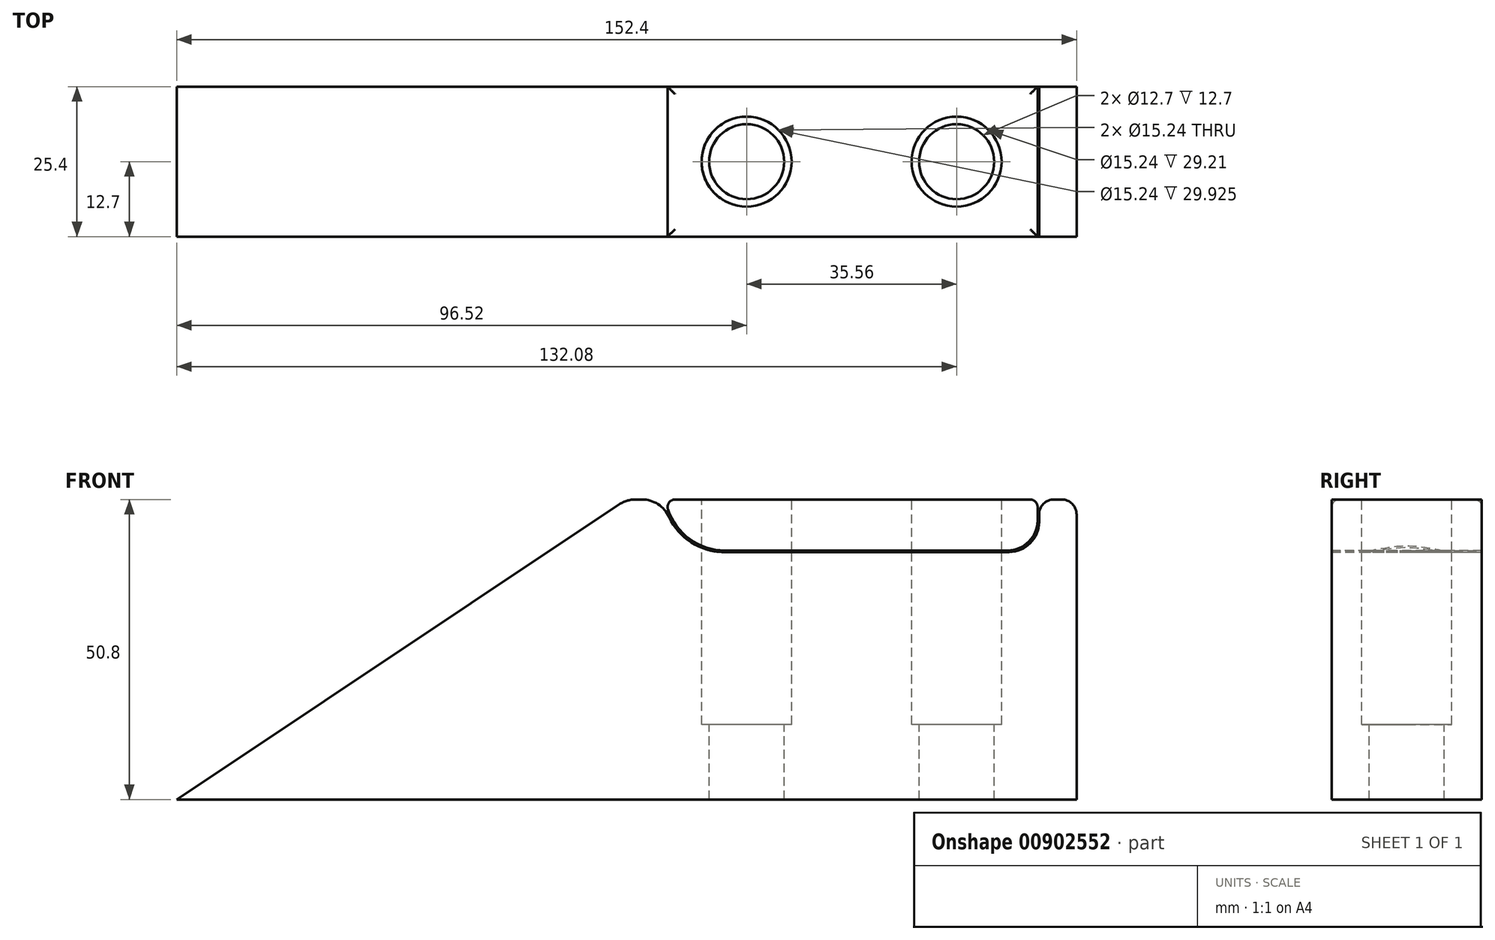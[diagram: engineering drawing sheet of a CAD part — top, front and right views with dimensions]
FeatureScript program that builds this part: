
annotation { "Feature Type Name" : "Feature", "Feature Type Description" : "" }
export const myFeature = defineFeature(function(context is Context, id is Id, definition is map)
    precondition{}
    {
        {
            var Q0;
            Q0=qCreatedBy(makeId("Front.planeOp"),FACE);
            var sketch = newSketch(context, id + "F0", { "sketchPlane" : qUnion([Q0])});
            skLineSegment(sketch, "E0.bottom", {"start": v(-76.2, -25.4) * mm, "end": v(76.2, -25.4) * mm});
            skLineSegment(sketch, "E0.right", {"start": v(76.2, -25.4) * mm, "end": v(76.2, 25.4) * mm});
            skPoint(sketch, "E0.middle", {"position": v(0, 0) * mm});
            skLineSegment(sketch, "E1", {"start": v(-76.2, -25.4) * mm, "end": v(0, 25.4) * mm});
            skLineSegment(sketch, "E2", {"start": v(6.35, 25.4) * mm, "end": v(6.35, 16.5) * mm});
            skLineSegment(sketch, "E3", {"start": v(6.35, 16.5) * mm, "end": v(69.85, 16.51) * mm});
            skLineSegment(sketch, "E4", {"start": v(69.85, 16.51) * mm, "end": v(69.85, 25.4) * mm});
            skLineSegment(sketch, "E5", {"start": v(0, 25.4) * mm, "end": v(6.35, 25.4) * mm});
            skLineSegment(sketch, "E6", {"start": v(69.85, 25.4) * mm, "end": v(76.2, 25.4) * mm});
            skLineSegment(sketch, "E7", {"start": v(6.6, 25.4) * mm, "end": v(6.6, 16.76) * mm});
            skLineSegment(sketch, "E8", {"start": v(6.6, 16.76) * mm, "end": v(69.6, 16.76) * mm});
            skLineSegment(sketch, "E9", {"start": v(69.6, 16.76) * mm, "end": v(69.6, 25.4) * mm});
            skLineSegment(sketch, "E10", {"start": v(6.6, 25.4) * mm, "end": v(69.6, 25.4) * mm});
            skSolve(sketch);
        }
        {
            var Q0;
            Q0=qSketchRegion(id+"F0",true);
            var Q1;
            Q1=makeQuery(id+"F0.imprint","IMPRINT",FACE,{"disambiguationData":[TD([[makeQuery(id+"F0.imprint","IMPRINT",EDGE,{"derivedFrom":sQuery(id+"F0.wireOp",EDGE,"E0.bottom")}),1.0]])]});
            extrude(context, id + "F1", {"entities" : qUnion([Q0, Q1]), "endBound" : BoundingType.SYMMETRIC, "depth" : 25.4 * mm, "offsetDistance" : 25.4 * mm});
        }
        {
            var Q0;
            Q0=makeQuery(id+"F1.opExtrude","SWEPT_FACE",FACE,{"disambiguationData":[OSD([sQuery(id+"F0.wireOp",EDGE,"E10")])]});
            var sketch = newSketch(context, id + "F2", { "sketchPlane" : qUnion([Q0])});
            skCircle(sketch, "E11", {"center": v(20.32, 0) * mm, "radius": 7.62 * mm});
            skCircle(sketch, "E12", {"center": v(55.88, 0) * mm, "radius": 7.62 * mm});
            skSolve(sketch);
        }
        {
            var Q0;
            Q0=makeQuery(id+"F2.imprint","IMPRINT",FACE,{"disambiguationData":[TD([[makeQuery(id+"F2.imprint","IMPRINT",EDGE,{"derivedFrom":sQuery(id+"F2.wireOp",EDGE,"E11")}),1.0]])]});
            var Q1;
            Q1=makeQuery(id+"F2.imprint","IMPRINT",FACE,{"disambiguationData":[TD([[makeQuery(id+"F2.imprint","IMPRINT",EDGE,{"derivedFrom":sQuery(id+"F2.wireOp",EDGE,"E12")}),1.0]])]});
            extrude(context, id + "F3", {"entities" : qUnion([Q0, Q1]), "operationType" : NewBodyOperationType.REMOVE, "oppositeDirection" : true, "depth" : 38.1 * mm, "offsetDistance" : 25.4 * mm});
        }
        {
            var Q0;
            Q0=makeQuery(id+"F1.opExtrude","SWEPT_FACE",FACE,{"disambiguationData":[OSD([sQuery(id+"F0.wireOp",EDGE,"E3")])]});
            var sketch = newSketch(context, id + "F4", { "sketchPlane" : qUnion([Q0])});
            skCircle(sketch, "E13", {"center": v(20.32, 0) * mm, "radius": 6.35 * mm});
            skCircle(sketch, "E14", {"center": v(55.88, 0) * mm, "radius": 6.35 * mm});
            skSolve(sketch);
        }
        {
            var Q0;
            Q0=makeQuery(id+"F4.imprint","IMPRINT",FACE,{"disambiguationData":[TD([[makeQuery(id+"F4.imprint","IMPRINT",EDGE,{"derivedFrom":sQuery(id+"F4.wireOp",EDGE,"E13")}),1.0]])]});
            var Q1;
            Q1=makeQuery(id+"F4.imprint","IMPRINT",FACE,{"disambiguationData":[TD([[makeQuery(id+"F4.imprint","IMPRINT",EDGE,{"derivedFrom":sQuery(id+"F4.wireOp",EDGE,"E14")}),1.0]])]});
            extrude(context, id + "F5", {"entities" : qUnion([Q0, Q1]), "operationType" : NewBodyOperationType.REMOVE, "oppositeDirection" : true, "depth" : 50.8 * mm, "offsetDistance" : 25.4 * mm});
        }
        {
            var Q0;
            Q0=makeQuery(id+"F1.opExtrude","SWEPT_EDGE",EDGE,{"disambiguationData":[OSD([sQuery(id+"F0.wireOp",EDGE,"E7"),sQuery(id+"F0.wireOp",EDGE,"E8")])]});
            fillet(context, id + "F6", {"entities" : qUnion([Q0]), "radius" : 10.16 * mm, "tangentPropagation" : true, "allowEdgeOverflow" : false});
        }
        {
            var Q0;
            Q0=makeQuery(id+"F1.opExtrude","SWEPT_EDGE",EDGE,{"disambiguationData":[OSD([sQuery(id+"F0.wireOp",EDGE,"E2"),sQuery(id+"F0.wireOp",EDGE,"E3")])]});
            fillet(context, id + "F7", {"entities" : qUnion([Q0]), "radius" : 10.16 * mm, "tangentPropagation" : true, "allowEdgeOverflow" : false});
        }
        {
            var Q0;
            Q0=makeQuery(id+"F7.opFillet","BLEND_EDGE",EDGE,{"blendedFrom":[makeQuery(id+"F1.opExtrude","SWEPT_EDGE",EDGE,{"disambiguationData":[OSD([sQuery(id+"F0.wireOp",EDGE,"E2"),sQuery(id+"F0.wireOp",EDGE,"E3")])]}),makeQuery(id+"F1.opExtrude","SWEPT_FACE",FACE,{"disambiguationData":[OSD([sQuery(id+"F0.wireOp",EDGE,"E5")])]})],"blendedInto":[makeQuery(id+"F1.opExtrude","SWEPT_FACE",FACE,{"disambiguationData":[OSD([sQuery(id+"F0.wireOp",EDGE,"E5")])]})]});
            var Q1;
            Q1=makeQuery(id+"F1.opExtrude","SWEPT_EDGE",EDGE,{"disambiguationData":[OSD([sQuery(id+"F0.wireOp",EDGE,"E1"),sQuery(id+"F0.wireOp",EDGE,"E5")])]});
            fillet(context, id + "F8", {"entities" : qUnion([Q0, Q1]), "radius" : 5.08 * mm, "tangentPropagation" : true, "allowEdgeOverflow" : false});
        }
        {
            var Q0;
            Q0=makeQuery(id+"F1.opExtrude","SWEPT_EDGE",EDGE,{"disambiguationData":[OSD([sQuery(id+"F0.wireOp",EDGE,"E0.right"),sQuery(id+"F0.wireOp",EDGE,"E6")])]});
            var Q1;
            Q1=makeQuery(id+"F1.opExtrude","SWEPT_EDGE",EDGE,{"disambiguationData":[OSD([sQuery(id+"F0.wireOp",EDGE,"E4"),sQuery(id+"F0.wireOp",EDGE,"E6")])]});
            fillet(context, id + "F9", {"entities" : qUnion([Q0, Q1]), "radius" : 2.54 * mm, "tangentPropagation" : true, "allowEdgeOverflow" : false});
        }
        {
            var Q0;
            Q0=makeQuery(id+"F1.opExtrude","SWEPT_EDGE",EDGE,{"disambiguationData":[OSD([sQuery(id+"F0.wireOp",EDGE,"E8"),sQuery(id+"F0.wireOp",EDGE,"E9")])]});
            fillet(context, id + "F10", {"entities" : qUnion([Q0]), "radius" : 5.08 * mm, "tangentPropagation" : true, "allowEdgeOverflow" : false});
        }
        {
            var Q0;
            Q0=makeQuery(id+"F1.opExtrude","SWEPT_EDGE",EDGE,{"disambiguationData":[OSD([sQuery(id+"F0.wireOp",EDGE,"E3"),sQuery(id+"F0.wireOp",EDGE,"E4")])]});
            fillet(context, id + "F11", {"entities" : qUnion([Q0]), "radius" : 5.08 * mm, "tangentPropagation" : true, "allowEdgeOverflow" : false});
        }
        {
            var Q0;
            Q0=makeQuery(id+"F1.opExtrude","CAP_EDGE",EDGE,{"disambiguationData":[OSD([sQuery(id+"F0.wireOp",EDGE,"E10")])],"isStart":true});
            var Q1;
            Q1=makeQuery(id+"F1.opExtrude","CAP_EDGE",EDGE,{"disambiguationData":[OSD([sQuery(id+"F0.wireOp",EDGE,"E10")])],"isStart":false});
            var Q2;
            Q2=makeQuery(id+"F1.opExtrude","SWEPT_EDGE",EDGE,{"disambiguationData":[OSD([sQuery(id+"F0.wireOp",EDGE,"E9"),sQuery(id+"F0.wireOp",EDGE,"E10")])]});
            var Q3;
            Q3=makeQuery(id+"F6.opFillet","BLEND_EDGE",EDGE,{"blendedFrom":[makeQuery(id+"F1.opExtrude","SWEPT_EDGE",EDGE,{"disambiguationData":[OSD([sQuery(id+"F0.wireOp",EDGE,"E7"),sQuery(id+"F0.wireOp",EDGE,"E8")])]}),makeQuery(id+"F1.opExtrude","SWEPT_FACE",FACE,{"disambiguationData":[OSD([sQuery(id+"F0.wireOp",EDGE,"E10")])]})],"blendedInto":[makeQuery(id+"F1.opExtrude","SWEPT_FACE",FACE,{"disambiguationData":[OSD([sQuery(id+"F0.wireOp",EDGE,"E10")])]})]});
            fillet(context, id + "F12", {"entities" : qUnion([Q0, Q1, Q2, Q3]), "radius" : 1.27 * mm, "tangentPropagation" : true, "allowEdgeOverflow" : false});
        }
    });
